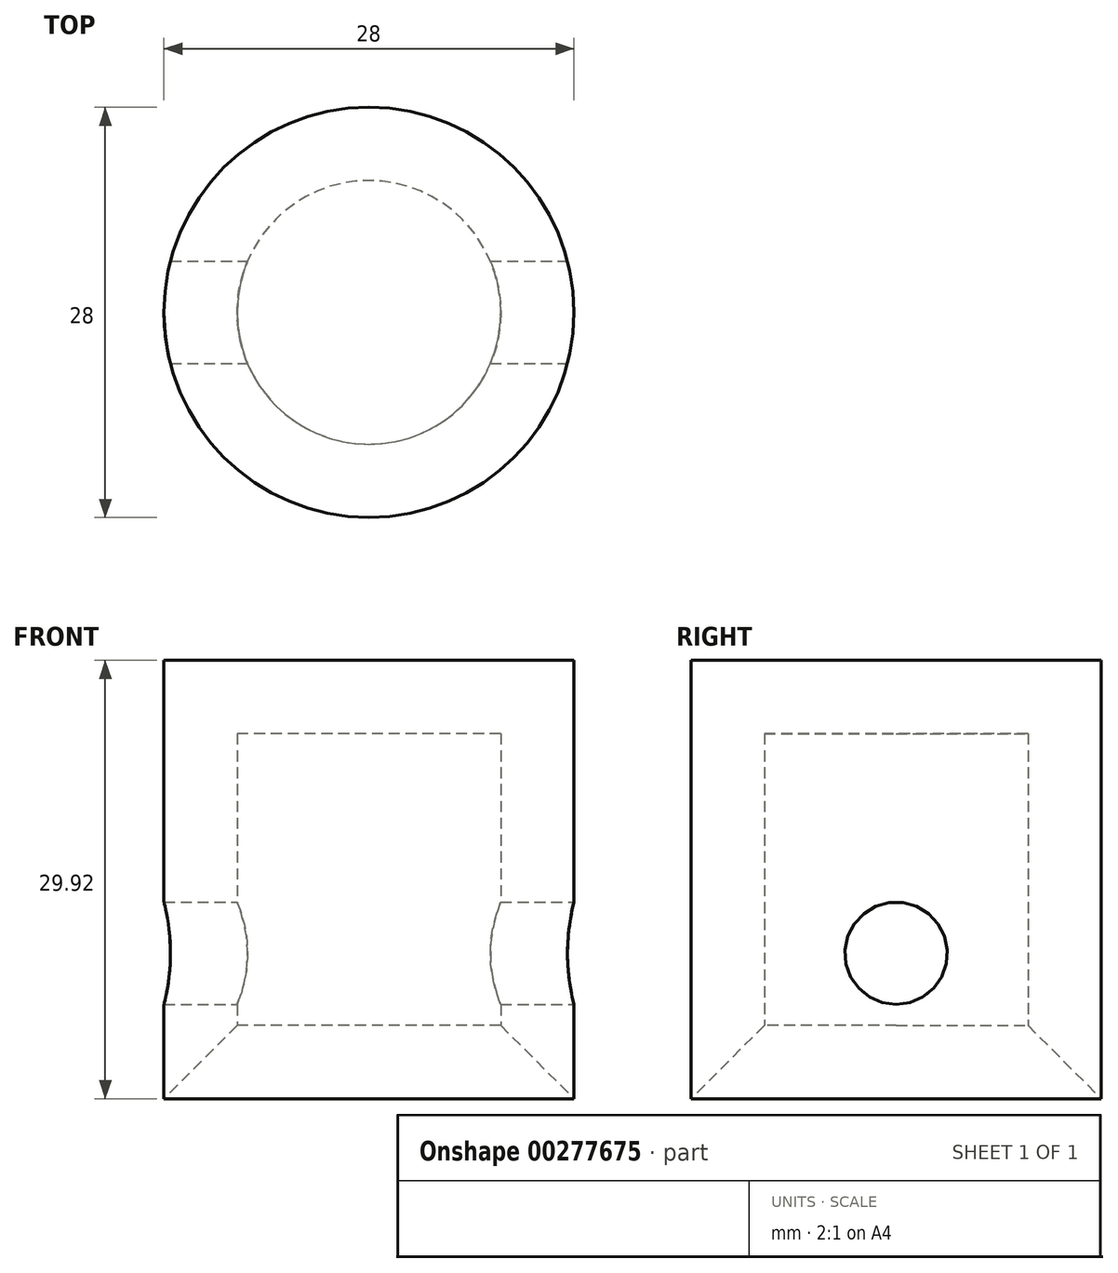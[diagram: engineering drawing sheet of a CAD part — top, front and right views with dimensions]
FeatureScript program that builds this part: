
annotation { "Feature Type Name" : "Feature", "Feature Type Description" : "" }
export const myFeature = defineFeature(function(context is Context, id is Id, definition is map)
    precondition{}
    {
        {
            var Q0;
            Q0=qCreatedBy(makeId("Top.planeOp"),FACE);
            var sketch = newSketch(context, id + "F0", { "sketchPlane" : qUnion([Q0])});
            skCircle(sketch, "E0", {"center": v(0, 0) * mm, "radius": 14 * mm});
            skSolve(sketch);
        }
        {
            var Q0;
            Q0 = qSketchRegion(id + "F0", true);
            extrude(context, id + "F1", {"entities" : qUnion([Q0]), "depth" : 30 * mm});
        }
        {
            var Q0;
            Q0=makeQuery(id+"F1.opExtrude","CAP_FACE",FACE,{"disambiguationData":[OSD([sQuery(id+"F0.wireOp",EDGE,"E0")])],"isStart":true});
            shell(context, id + "F2", {"entities" : qUnion([Q0]), "thickness" : 5 * mm});
        }
        {
            var Q0;
            Q0=qCreatedBy(makeId("Right.planeOp"),FACE);
            var sketch = newSketch(context, id + "F3", { "sketchPlane" : qUnion([Q0])});
            skCircle(sketch, "E1", {"center": v(0, 10) * mm, "radius": 3.5 * mm});
            skSolve(sketch);
        }
        {
            var Q0;
            Q0 = qSketchRegion(id + "F3", true);
            extrude(context, id + "F4", {"entities" : qUnion([Q0]), "operationType" : NewBodyOperationType.REMOVE, "endBound" : BoundingType.THROUGH_ALL, "oppositeDirection" : true, "depth" : 25.4 * mm, "hasSecondDirection" : true, "secondDirectionBound" : SecondDirectionBoundingType.THROUGH_ALL, "secondDirectionOppositeDirection" : false, "secondDirectionDepth" : 25.4 * mm});
        }
        {
            var Q0;
            {var subQ0=sQuery(id+"F0.wireOp",EDGE,"E0");Q0=makeQuery(id+"F2.opShell","OFFSET_EDGE",EDGE,{"disambiguationData":[OSD([subQ0]),TDD([makeQuery(id+"F1.opExtrude","CAP_EDGE",EDGE,{"disambiguationData":[OSD([subQ0])],"isStart":true})])]});}
            chamfer(context, id + "F5", {"entities" : qUnion([Q0]), "width" : 5.08 * mm, "tangentPropagation" : true});
        }
    });
